# Revit family: 71_98_0505+0515_NESTED
name_source: partatom
category: Communication Devices
revit_build: Autodesk Revit 2015 (Build: 20141119_1515(x64)
units: mm (PartAtom-declared; Revit-internal decimal feet)

## types (6) — shared parameters
Basisplaat = Basisplaat
Breedte = 50 mm  [stored 0.164042 ft]
Consumption = 3 W
Default Elevation = 1219 mm
Diepte = 84 mm  [stored 0.275591 ft]
Frequency response = 20 Hz
Jack = Jack
Knoppen = Basisplaat
Lengte = 155 mm  [stored 0.50853 ft]
Manufacturer = Televic Conference
Onderplaat = Inox
Scherm = Jack
Schroef = Basisplaat
THD @ nominal level = 0.1 %
URL = http://www.televic-conference.com
Voltage = 48 V
Weight = 280

## per-type parameters (varying)
| type | Dynamic range | Flexible microphone - 71.03.3540 | Microphone - 71.03.3140 | Model | Product ID | Type 71.98.0515 | Type Comments |
| Type 71.98.0505 - flexible microphone | > 90 dB | Yes | No | Confidea F-DM | 71.98.0505 | No | Confidea Flushmount Delegate Microphone Unit |
| Type 71.98.0505 - microphone | > 90 dB | No | Yes | Confidea F-DM | 71.98.0505 | No | Confidea Flushmount Delegate Microphone Unit |
| Type 71.98.0505 - no microphone | > 90 dB | No | No | Confidea F-DM | 71.98.0505 | No | Confidea Flushmount Delegate Microphone Unit |
| Type 71.98.0515 - flexible microphone | > 90 bD | Yes | No | Confidea F-CM | 71.98.0515 | Yes | Confidea Flushmount Chairman Microphone Unit |
| Type 71.98.0515 - microphone | > 90 dB | No | Yes | Confidea F-CM | 71.98.0515 | Yes | Confidea Flushmount Chairman Microphone Unit |
| Type 71.98.0515 - no microphone | > 90 bD | No | No | Confidea F-CM | 71.98.0515 | Yes | Confidea Flushmount Chairman Microphone Unit |

note: [stored X ft] marks values corroborated as IEEE doubles in the binary element streams (Revit-internal decimal feet)

## geometry (parser evidence)
native form markers: Sweep x11
no freeform markers — native parametric forms only
